FCSTD DOCUMENT  (FreeCAD 0.20R29177 +426 (Git))
Label: Ensamble
License: All rights reserved
LicenseURL: http://en.wikipedia.org/wiki/All_rights_reserved
objects: PartDesign::CoordinateSystem×4, App::DocumentObjectGroup×3, App::Link×3, App::Part×2, App::FeaturePython×1, Sketcher::SketchObject×1
note: 5 computed .brp shape members not serialized (recipe doc carries the construction recipe); baked Part::Feature solids carry a one-line shape summary decoded from their .brp
EXTERNAL_REF file=brazo.FCStd obj=BrazoLCS
EXTERNAL_REF file=brazo.FCStd obj=Body

FEATURE [PartDesign::CoordinateSystem] LCS_Origin
  AttacherType = Attacher::AttachEngine3D
  MapMode = 2
  Support = -> [X_Axis]
FEATURE [App::DocumentObjectGroup] Constraints
FEATURE [App::FeaturePython] Variables  # WARN: FeaturePython — macro-defined, semantics opaque (R4)
  Type = App::PropertyContainer
FEATURE [App::DocumentObjectGroup] Configurations
FEATURE [PartDesign::CoordinateSystem] LCS_0
  AttacherType = Attacher::AttachEngine3D
  MapMode = 2
  Support = -> [X_Axis001]
FEATURE [Sketcher::SketchObject] EsqueletoSketch
  FullyConstrained = false
  sketch-geometry (4):
    g0: LineSegment StartX=-32.1585 StartY=0 StartZ=0 EndX=32.1585 EndY=76.5724 EndZ=0
    g1: GeomPoint X=0 Y=38.2862 Z=0
    g2: LineSegment StartX=32.1585 StartY=0 StartZ=0 EndX=-32.1585 EndY=76.5724 EndZ=0
    g3: GeomPoint X=0 Y=38.2862 Z=0
  constraints (8):
    c: Symmetric(g0,g0,g1)
    c: Distance(g0,g0) = 100
    c: Symmetric(g2,g2,g3)
    c: Distance(g2,g2) = 100
    c: Coincident(g3,g1)
    c: PointOnObject(g1,g-2)
    c: PointOnObject(g0,g-1)
    c: PointOnObject(g2,g-1)
FEATURE [PartDesign::CoordinateSystem] Brazo1_LCS  label="Brazo1-LCS"
  AttacherType = Attacher::AttachEngine3D
  MapMode = 45
  Placement = pos=(-3.6e-15,38.2862,0) rot=(0.249425,0.684758,0.684758;2.65272rad)
  Support = -> [EsqueletoSketch]
FEATURE [App::Part] EsqueletoPart
  Group = -> [LCS_0,EsqueletoSketch,Brazo1_LCS]
  Origin = -> Origin001
FEATURE [App::DocumentObjectGroup] Parts
  Group = -> [EsqueletoPart]
FEATURE [PartDesign::CoordinateSystem] Brazo2_LCS  label="Brazo2-LCS"
  AttacherType = Attacher::AttachEngine3D
  MapMode = 45
  Placement = pos=(-3.6e-15,38.2862,0) rot=(-0.249425,0.684758,0.684758;3.63047rad)
  Support = -> [EsqueletoSketch]
FEATURE [App::Link] EsqueletoPart001
  AttachedBy = #LCS_0
  AttachedTo = Parent Assembly#LCS_Origin
  AttachmentOffset = pos=(0,0,0) rot=(1,0,0;1.5708rad)
  LinkPlacement = pos=(0,0,0) rot=(1,0,0;1.5708rad)
  LinkedObject = -> EsqueletoPart
  Placement = pos=(0,0,0) rot=(1,0,0;1.5708rad)
  SolverId = Asm4EE
  expr: Placement = LCS_Origin.Placement * AttachmentOffset * LCS_0.Placement ^ -1
FEATURE [App::Link] Body
  AttachedBy = #BrazoLCS
  AttachedTo = Parent Assembly#Brazo2_LCS
  LinkPlacement = pos=(1.60792,36.3719,-3e-16) rot=(-0.671586,0.312962,0.671586;2.53498rad)
  LinkedObject = -> <external brazo.FCStd>#Body
  Placement = pos=(1.60792,36.3719,-3e-16) rot=(-0.671586,0.312962,0.671586;2.53498rad)
  SolverId = Asm4EE
  expr: Placement = Brazo2_LCS.Placement * AttachmentOffset * brazo#BrazoLCS.Placement ^ -1
FEATURE [App::Link] Body001
  AttachedBy = #BrazoLCS
  AttachedTo = Parent Assembly#Brazo2_LCS
  AttachmentOffset = pos=(0,0,0) rot=(0.707107,0.707107,0;3.14159rad)
  LinkPlacement = pos=(-1.60792,40.2005,1e-16) rot=(-0.888982,-0.323814,-0.323814;4.59498rad)
  LinkedObject = -> <external brazo.FCStd>#Body
  Placement = pos=(-1.60792,40.2005,1e-16) rot=(-0.888982,-0.323814,-0.323814;4.59498rad)
  SolverId = Asm4EE
  expr: Placement = Brazo2_LCS.Placement * AttachmentOffset * brazo#BrazoLCS.Placement ^ -1
FEATURE [App::Part] Assembly
  AssemblyType = Part::Link
  Group = -> [LCS_Origin,Constraints,Variables,Configurations,Brazo2_LCS,EsqueletoPart001,Body,Body001]
  Origin = -> Origin
  Type = Assembly
